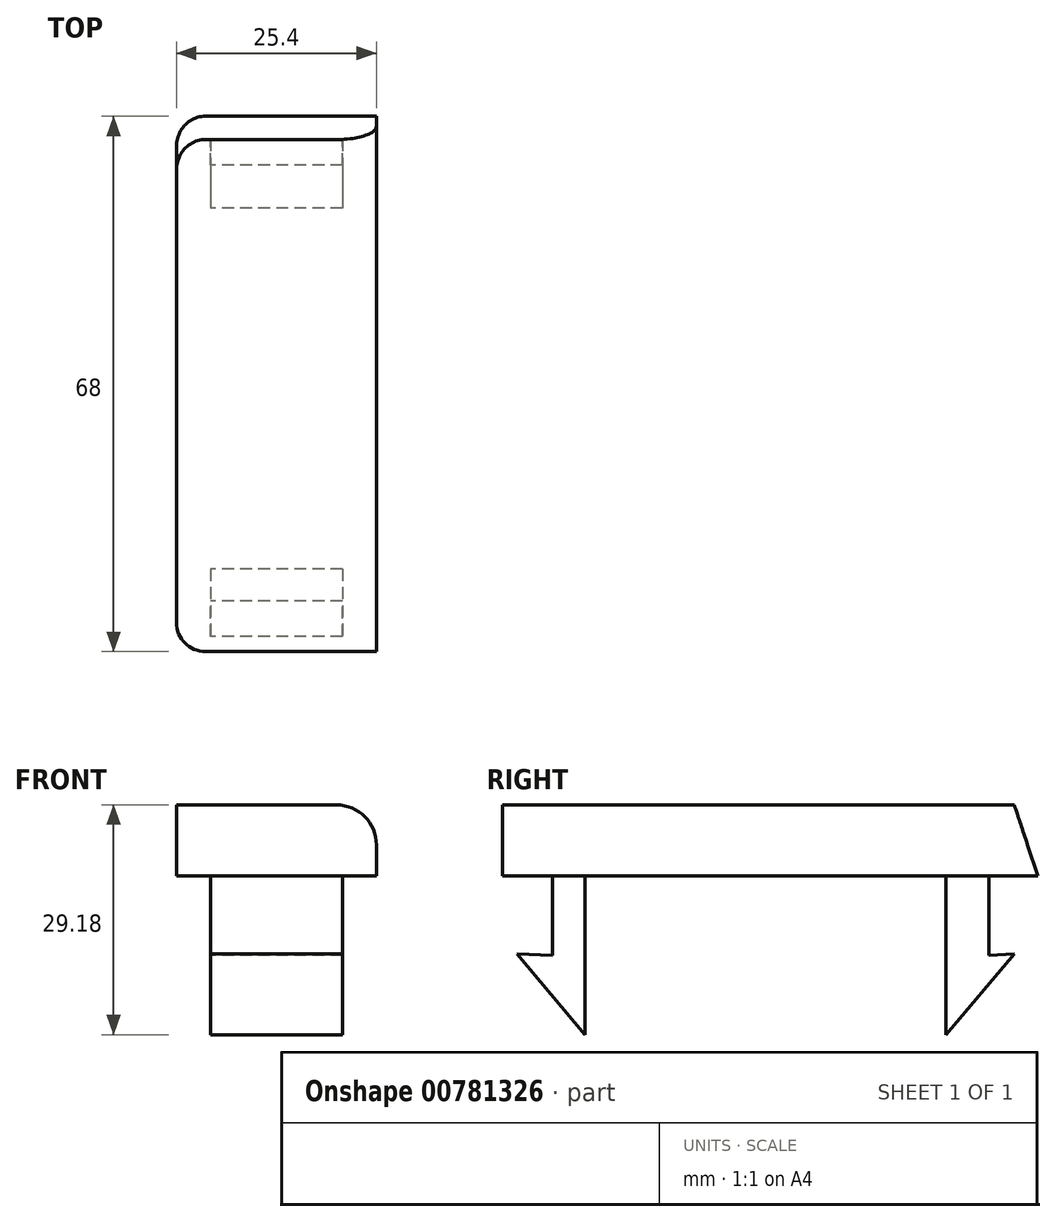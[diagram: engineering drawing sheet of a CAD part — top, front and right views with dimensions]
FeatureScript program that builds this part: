
annotation { "Feature Type Name" : "Feature", "Feature Type Description" : "" }
export const myFeature = defineFeature(function(context is Context, id is Id, definition is map)
    precondition{}
    {
        {
            var Q0;
            Q0=qCreatedBy(makeId("Right.planeOp"),FACE);
            var sketch = newSketch(context, id + "F0", { "sketchPlane" : qUnion([Q0])});
            skLineSegment(sketch, "E0", {"start": v(-34.37, 31.4) * mm, "end": v(30.3, 31.4) * mm});
            skLineSegment(sketch, "E1", {"start": v(30.3, 31.4) * mm, "end": v(33.28, 22.4) * mm});
            skLineSegment(sketch, "E2", {"start": v(33.28, 22.4) * mm, "end": v(27.08, 22.4) * mm});
            skLineSegment(sketch, "E3", {"start": v(27.08, 22.4) * mm, "end": v(27.08, 12.3) * mm});
            skLineSegment(sketch, "E4", {"start": v(27.08, 12.3) * mm, "end": v(30.3, 12.5) * mm});
            skLineSegment(sketch, "E5", {"start": v(30.3, 12.5) * mm, "end": v(21.6, 2.21) * mm});
            skLineSegment(sketch, "E6", {"start": v(21.6, 2.21) * mm, "end": v(21.6, 22.4) * mm});
            skLineSegment(sketch, "E7", {"start": v(21.6, 22.4) * mm, "end": v(1.61, 22.4) * mm});
            skLineSegment(sketch, "E8", {"start": v(1.61, 22.4) * mm, "end": v(-9.07, 22.4) * mm});
            skLineSegment(sketch, "E9", {"start": v(-9.07, 22.4) * mm, "end": v(-20.55, 22.4) * mm});
            skLineSegment(sketch, "E10", {"start": v(-20.55, 22.4) * mm, "end": v(-24.26, 22.4) * mm});
            skLineSegment(sketch, "E11", {"start": v(-24.26, 22.4) * mm, "end": v(-24.26, 2.21) * mm});
            skLineSegment(sketch, "E12", {"start": v(-24.26, 2.21) * mm, "end": v(-32.85, 12.5) * mm});
            skLineSegment(sketch, "E13", {"start": v(-32.85, 12.5) * mm, "end": v(-28.33, 12.3) * mm});
            skLineSegment(sketch, "E14", {"start": v(-28.33, 12.3) * mm, "end": v(-28.33, 22.4) * mm});
            skLineSegment(sketch, "E15", {"start": v(-28.33, 22.4) * mm, "end": v(-34.72, 22.4) * mm});
            skLineSegment(sketch, "E16", {"start": v(-34.72, 22.4) * mm, "end": v(-34.72, 31.4) * mm});
            skLineSegment(sketch, "E17", {"start": v(-34.72, 31.4) * mm, "end": v(-34.37, 31.4) * mm});
            skLineSegment(sketch, "E18", {"start": v(27.08, 22.4) * mm, "end": v(21.6, 22.4) * mm});
            skLineSegment(sketch, "E19", {"start": v(-24.26, 22.4) * mm, "end": v(-28.33, 22.4) * mm});
            skPoint(sketch, "E20", {"position": v(-24.26, 12.3) * mm});
            skSolve(sketch);
        }
        {
            var Q0;
            Q0=makeQuery(id+"F0.imprint","IMPRINT",FACE,{"disambiguationData":[TD([[makeQuery(id+"F0.imprint","IMPRINT",EDGE,{"derivedFrom":sQuery(id+"F0.wireOp",EDGE,"E0")}),-1.0]])]});
            extrude(context, id + "F1", {"entities" : qUnion([Q0]), "endBound" : BoundingType.SYMMETRIC, "depth" : 25.4 * mm, "offsetDistance" : 25.4 * mm});
        }
        {
            var Q0;
            Q0 = qSketchRegion(id + "F0", true);
            extrude(context, id + "F2", {"entities" : qUnion([Q0]), "operationType" : NewBodyOperationType.ADD, "endBound" : BoundingType.SYMMETRIC, "depth" : 16.76 * mm, "offsetDistance" : 25.4 * mm});
        }
        {
            var Q0;
            Q0=makeQuery(id+"F1.opExtrude","CAP_EDGE",EDGE,{"disambiguationData":[OSD([sQuery(id+"F0.wireOp",EDGE,"E16")])],"isStart":true});
            var Q1;
            Q1=makeQuery(id+"F1.opExtrude","CAP_EDGE",EDGE,{"disambiguationData":[OSD([sQuery(id+"F0.wireOp",EDGE,"E1")])],"isStart":true});
            fillet(context, id + "F3", {"entities" : qUnion([Q0, Q1]), "radius" : 3.68 * mm, "tangentPropagation" : true, "allowEdgeOverflow" : false});
        }
        {
            var Q0;
            Q0=makeQuery(id+"F1.opExtrude","CAP_EDGE",EDGE,{"disambiguationData":[OSD([sQuery(id+"F0.wireOp",EDGE,"E0"),sQuery(id+"F0.wireOp",EDGE,"E17")])],"isStart":false});
            fillet(context, id + "F4", {"entities" : qUnion([Q0]), "radius" : 5.08 * mm, "tangentPropagation" : true, "allowEdgeOverflow" : false});
        }
    });
